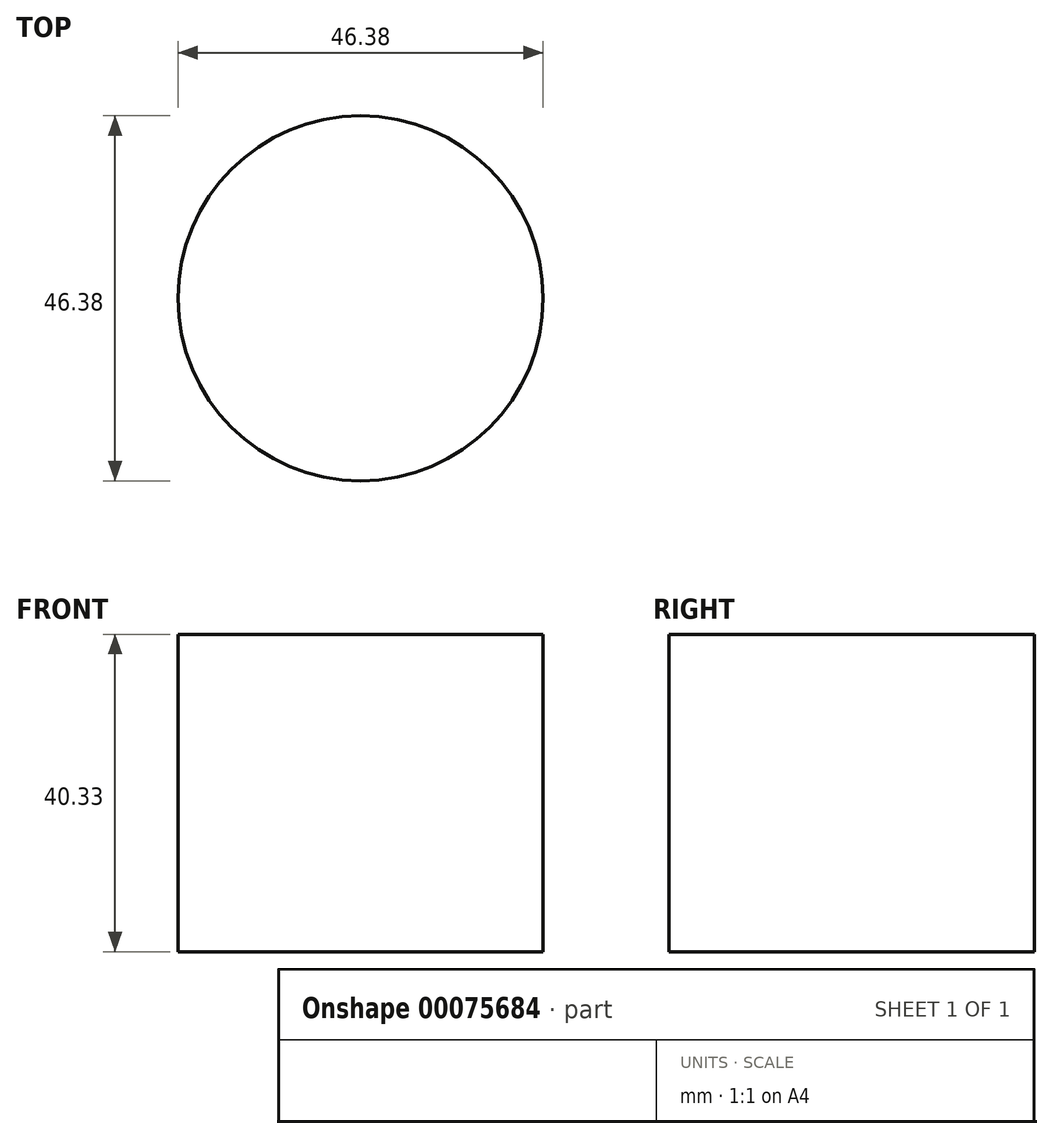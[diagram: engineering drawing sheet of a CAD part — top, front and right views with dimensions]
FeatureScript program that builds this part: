
annotation { "Feature Type Name" : "Feature", "Feature Type Description" : "" }
export const myFeature = defineFeature(function(context is Context, id is Id, definition is map)
    precondition{}
    {
        {
            var Q0;
            Q0=qCreatedBy(makeId("Top.planeOp"),FACE);
            var sketch = newSketch(context, id + "F0", { "sketchPlane" : qUnion([Q0])});
            skCircle(sketch, "E0", {"center": v(0, 0) * mm, "radius": 23.19 * mm});
            skSolve(sketch);
        }
        {
            var Q0;
            Q0=makeQuery(id+"F0.imprint","IMPRINT",FACE,{"disambiguationData":[TD([[makeQuery(id+"F0.imprint","IMPRINT",EDGE,{"derivedFrom":sQuery(id+"F0.wireOp",EDGE,"E0")}),1.0]])]});
            extrude(context, id + "F1", {"entities" : qUnion([Q0]), "depth" : 40.33 * mm});
        }
    });
